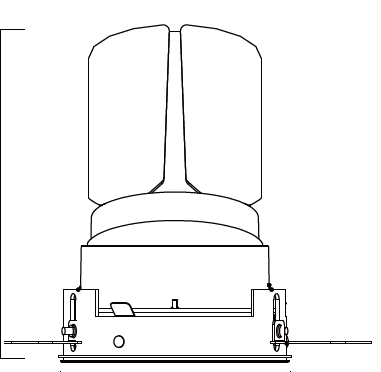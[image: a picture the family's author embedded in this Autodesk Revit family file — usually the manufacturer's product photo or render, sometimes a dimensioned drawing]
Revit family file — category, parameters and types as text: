
# Revit family: CORH05-R-DL-BK-WOT
name_source: partatom
category: Lighting Fixtures
units: mm (PartAtom-declared; Revit-internal decimal feet)

## family parameters
Cut with Voids When Loaded = Yes
Host = Face
Light Source = Yes
Maintain Annotation Orientation = No
Part Type = Normal
Room Calculation Point = No
Round Connector Dimension = Use Diameter
Shared = No

## types (8) — shared parameters
CRI = 90
Color Filter = 16777215
Default Elevation = 0' - 0"
Dimming Lamp Color Temperature Shift = <None>
Lamp = LED
Load Classification = Lighting
Manufacturer = Above All Lighting
Model = CORH05-R-DL-BK-WOT
Power Factor = 0.9
Tilt Angle = 90.00°
URL = https://www.abovealllighting.com

## per-type parameters (varying)
| type | Beam Angle | Photometric Web File | Wattage Comments |
| CORH05-R-DL-BK-WOT-30W-15D-3000K | 15.00° | CORH05-R-DL-30W-15D-3000K.IES | 30W |
| CORH05-R-DL-BK-WOT-30W-24D-3000K | 24.00° | CORH05-R-DL-30W-24D-3000K.IES | 30W |
| CORH05-R-DL-BK-WOT-30W-38D-3000K | 38.00° | CORH05-R-DL-30W-38D-3000K.IES | 30W |
| CORH05-R-DL-BK-WOT-30W-55D-3000K | 55.00° | CORH05-R-DL-30W-55D-3000K.IES | 30W |
| CORH05-R-DL-BK-WOT-35W-15D-3000K | 15.00° | CORH05-R-DL-35W-15D-3000K.IES | 35W |
| CORH05-R-DL-BK-WOT-35W-24D-3000K | 24.00° | CORH05-R-DL-35W-24D-3000K.IES | 35W |
| CORH05-R-DL-BK-WOT-35W-38D-3000K | 38.00° | CORH05-R-DL-35W-38D-3000K.IES | 35W |
| CORH05-R-DL-BK-WOT-35W-55D-3000K | 55.00° | CORH05-R-DL-35W-55D-3000K.IES | 35W |

## geometry (parser evidence)
native form markers: Sweep x11
no freeform markers — native parametric forms only
